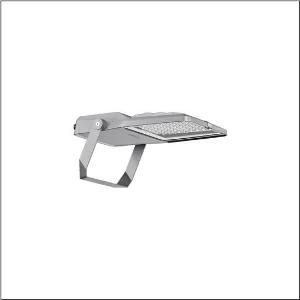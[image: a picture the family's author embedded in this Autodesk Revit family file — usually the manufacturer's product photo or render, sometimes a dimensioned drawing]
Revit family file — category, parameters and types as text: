
# Revit family: floodlight_fl_21_iq_mini___pl61_5xa7771d4c1a_f1b8
name_source: partatom
category: Lighting Fixtures
units: mm (PartAtom-declared; Revit-internal decimal feet)

## family parameters
Cut with Voids When Loaded = No
Host = Face
Light Source = No
Part Type = Normal
Room Calculation Point = No
Round Connector Dimension = Use Diameter
Shared = No

## types (1)
- --- (1 x LED, 18260 lm, 143 W, 4000K)
    Apparent Load = 143 VA
    CIE Flux Codes = 33 65 98 100 100
    Color Rendering = 70
    Color Temperature = 4000K
    Default Elevation = 1800 mm
    Description = Floodlight FL 21 iQ mini, floodlight, primary light control with lens, of PMMA, primary optical cover: protective disc, of toughened safety glass, transparent, light distribution: PL61, light emission: direct distribution, installation type: surface-mounted, LED, High Power LED, rated luminous flux: 18.260lm, luminous efficacy: 128lm/W, light colour: 740, colour temperature: 4000K, control: Auto-Match, Temp-Guard, Lumen-Switch, Night-Set, Smart-Wire, Light-Fading, Desk-Remote (wireless, voltage-free reading and setting of iQ features in the workshop via application-optimized NFC function/RFID function), optimised constant luminous flux control (CLO 2.0), with terminal, 6-pole, mains connection: 220..240V, AC, 50/60Hz, start of lifetime: 143W, end of service life: 152W, reduction: 61W, luminaire housing, of diecast aluminium, powder-coated, Siteco® metallic grey (DB 702S), corrosivity category C5 mid according to DIN EN ISO 12944, sealing non-destructively replaceable, mounting bracket, of steel, galvanised, powder-coated, Siteco® metallic grey (DB 702S), protection rating (complete): IP66, insulation class (complete): insulation class II (safety insulation), certification: CE, ENEC, VDE, protection symbol: D, impact resistance: IK08, permissible operating ambient temperature: -40..+40°C, permissible operating ambient temperature for outdoor applications: -40..+50°C, standard: DIN EN 12944, LABS conformity tested according to VDMA 24364:2018-05, packaging unit: 1 piece

Light Distribution: PL61
    Height = 70 mm
    Lamp = 1 x LED
    Lamp Light Flux = 18260 lm
    Lamp Power = 143 W
    Lamp count = 1
    Length = 485 mm
    Luminous efficacy = 128 lm/W
    Manufacturer = Siteco
    ModVariant = No
    Model = 5XA7771D4C1A
    Number of Poles = 1
    OnlyDefault = Yes
    Power Factor = 1
    Product Name = Floodlight FL 21 iQ mini | PL61
    Product group = floodlight | pylon annexe
    ProductGroupID = 6200
    Protection Class = Protection class II
    Protection Degree = IP 66
    RLX_Detail_Level = 1
    RLX_Emergency_Light_Flux = 0 lm
    RLX_Emergency_Type = 0
    RLX_Emergency_Type_DB = No
    RlxData = <blob elided: 96661 chars, md5=01923a01>
    Socket = socket
    Standby Power = 0 W
    System Light Flux = 18260 lm
    System Power = 143 W
    Type Comments = factory setting: luminous flux: 100 % | dim-lin: 254 | 730 mA
    Type Image = l_1006845.jpg
    URL = http://relux.com
    VarID = @adj_123607
    Voltage = 0 V
    Weight = 0.00 kg
    Width = 337 mm

## geometry (parser evidence)
native form markers: Blend x4, Sweep x13
no freeform markers — native parametric forms only
